# Revit family: Certus LED
name_source: partatom
category: Lighting Fixtures
revit_build: Autodesk Revit Architecture 2014 (Build: 20140709_2115(x64)
units: mm (PartAtom-declared; Revit-internal decimal feet)

## types (2) — shared parameters
Apparent Load = 240 VA
ArticleNumber = See URL hyperlink
AssetType = Moveable/Fixed
BSAB 96 = SNB.2
BallastsCELMAEnergyEfficiencyIndex = Class A1/A2
CCSClassCode = UAC
CCSClassName = Belysningsarmatur
CCSTopnode = L
Color Filter = 16777215
Colour = Grey backcover and stainless steel clips.
ControlGearPosition = Integrated
Description = 70-80-35 General Lighting Systems
Dimming Lamp Color Temperature Shift = <None>
DocumentReference = See URL hyperlink
Documentation = See URL hyperlink
Finish = Glassfibre and acrylic or polycarbonate.
Frame = Riegens_Glass_polyester mat
Frame Depth = 169 mm
HasProtectiveEarth = TRUE
Height 1 = 108 mm
IP_Code = IP65
IfcExportAs = IfcLightFixtureType'
IfcExportType = NOTDEFINED'
InsulationStandardClass = Class 1
InternalFuse = Only required in emergency versions
LampColourRenderingIndex = Ra>80
LampType = LED
LightFixtureMountingType = Surface or Suspended
LightFixturePlacingType = Ceiling
LightSource = LED 4000K
LuminairePowerFactor = >0,9
LuminaireType = Surface or Suspended Direct LED Luminaire
Manufacturer = Riegens A/S
ManufacturerURL = www.riegens.com
Material = Glassfibre polyester reinforced, Acrylic or PC and Stainless steel.
NominalVoltage = 220-240V
Offset from ceiling = 400 mm
Optic = Direct: Profiled clear front cover
PhaseReference = IEC recommendations
PhotometricPerformance = In accordance with BS EN 13032-1
ProductInformation = http://riegens.com
Shape = Rectangle
Tilt Angle = 90.00°
URL = http://riegens.com
Uniclass 1.4 = JY73
Uniclass2 = Pr_70_70_49_43 Light-Emitting Diode (LED) Luminaires
Version = v.1.0

## per-type parameters (varying)
| type | BIMObjectName | Fp | Frame Width | LampRating | ModelReference | Photometric Web File | Size | TotalWattage |
| Certus 60W LED | Certus LED 60W LED.rfa | 1140 mm | 1574 mm | 60W | Certus LED 60W LED | Certus LED 60W 4000K Prismatic diffuser PMMA IP65.ies | 108 x 1574 x 169 mm | Max. 60W |
| Certus 36W / 49W LED | Certus LED 36W / 49W LED.rfa | 840 mm | 1274 mm | 36W / 49W | Certus LED 36W / 49W LED.rfa | Certus LED 49W 4000K Prismatic diffuser PMMA IP65.ies | 108 x 1274 x 169 mm | Max. 36W / 49W |

note: column(s) folded — value = type name in every type: Model

## geometry (parser evidence)
native form markers: Sweep x4
no freeform markers — native parametric forms only
